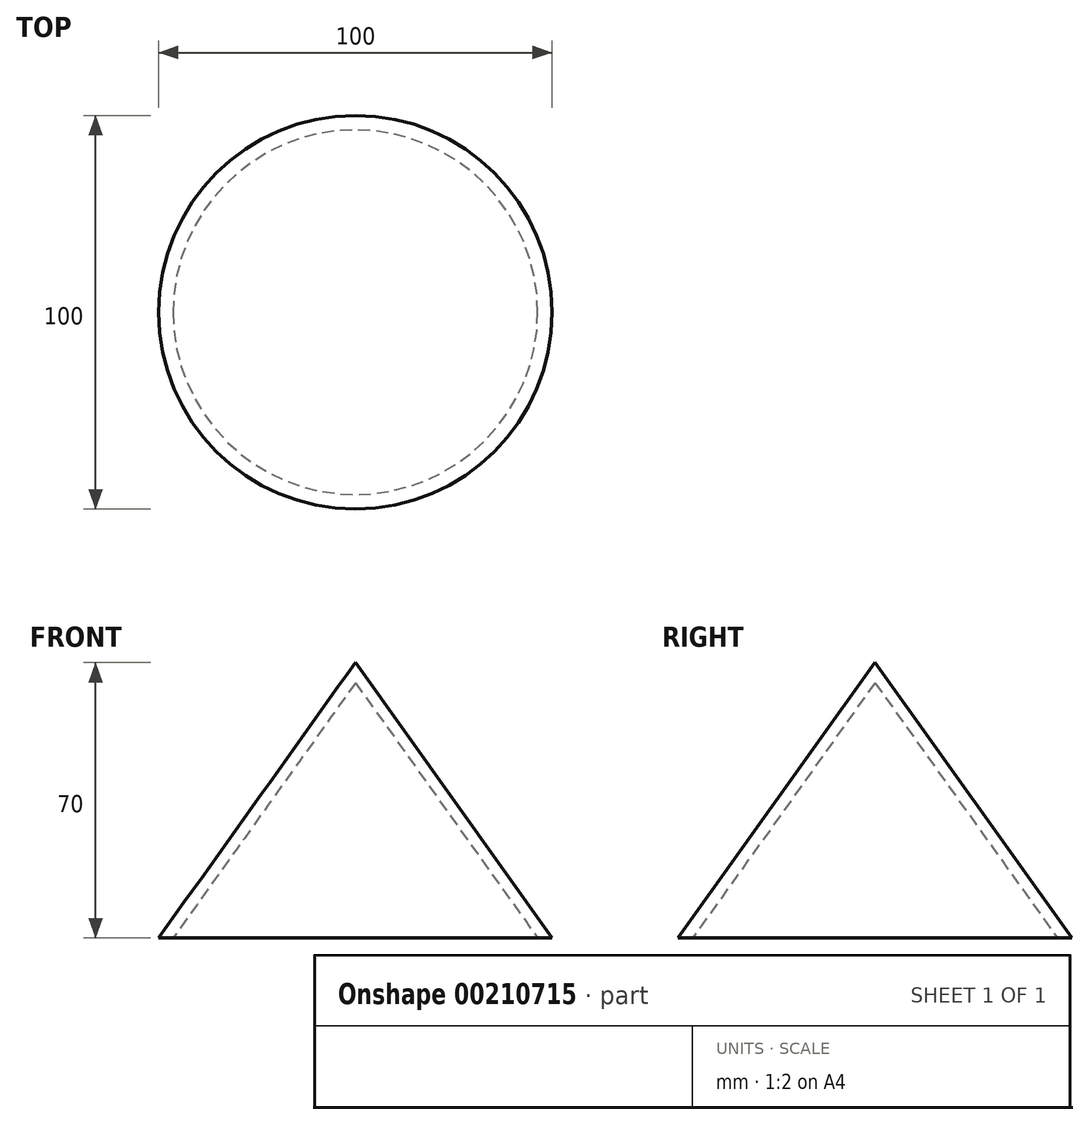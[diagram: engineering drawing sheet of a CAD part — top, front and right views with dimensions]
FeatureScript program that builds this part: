
annotation { "Feature Type Name" : "Feature", "Feature Type Description" : "" }
export const myFeature = defineFeature(function(context is Context, id is Id, definition is map)
    precondition{}
    {
        {
            var Q0;
            Q0=qCreatedBy(makeId("Top.planeOp"),FACE);
            var sketch = newSketch(context, id + "F0", { "sketchPlane" : qUnion([Q0])});
            skCircle(sketch, "E0", {"center": v(0, 0) * mm, "radius": 50 * mm});
            skSolve(sketch);
        }
        {
            var Q0;
            Q0=qCreatedBy(makeId("Top.planeOp"),FACE);
            cPlane(context, id + "F1", {"entities" : qUnion([Q0]), "cplaneType" : CPlaneType.OFFSET, "offset" : 70 * mm, "width" : 150 * mm, "height" : 150 * mm});
        }
        {
            var Q0;
            Q0=qCreatedBy(id+"F1.planeOp",FACE);
            var sketch = newSketch(context, id + "F2", { "sketchPlane" : qUnion([Q0])});
            skPoint(sketch, "E1", {"position": v(0, 0) * mm});
            skSolve(sketch);
        }
        {
            var Q0;
            Q0=makeQuery(id+"F0.imprint","IMPRINT",FACE,{"disambiguationData":[TD([[makeQuery(id+"F0.imprint","IMPRINT",EDGE,{"derivedFrom":sQuery(id+"F0.wireOp",EDGE,"E0")}),1.0]])]});
            var Q1;
            Q1=sQuery(id+"F2.wireOp",VERTEX,"E1");
            loft(context, id + "F3", {"sheetProfilesArray" : [{ "sheetProfileEntities" : qUnion([Q0]) }, { "sheetProfileEntities" : qUnion([Q1]) }]});
        }
        {
            var Q0;
            Q0=makeQuery(id+"F3.opLoft","CAP_FACE",FACE,{"disambiguationData":[OSD([makeQuery(id+"F0.imprint","IMPRINT",FACE,{"disambiguationData":[TD([[makeQuery(id+"F0.imprint","IMPRINT",EDGE,{"derivedFrom":sQuery(id+"F0.wireOp",EDGE,"E0")}),1.0]])]})])],"isStart":true});
            shell(context, id + "F4", {"entities" : qUnion([Q0]), "thickness" : 3 * mm});
        }
    });
